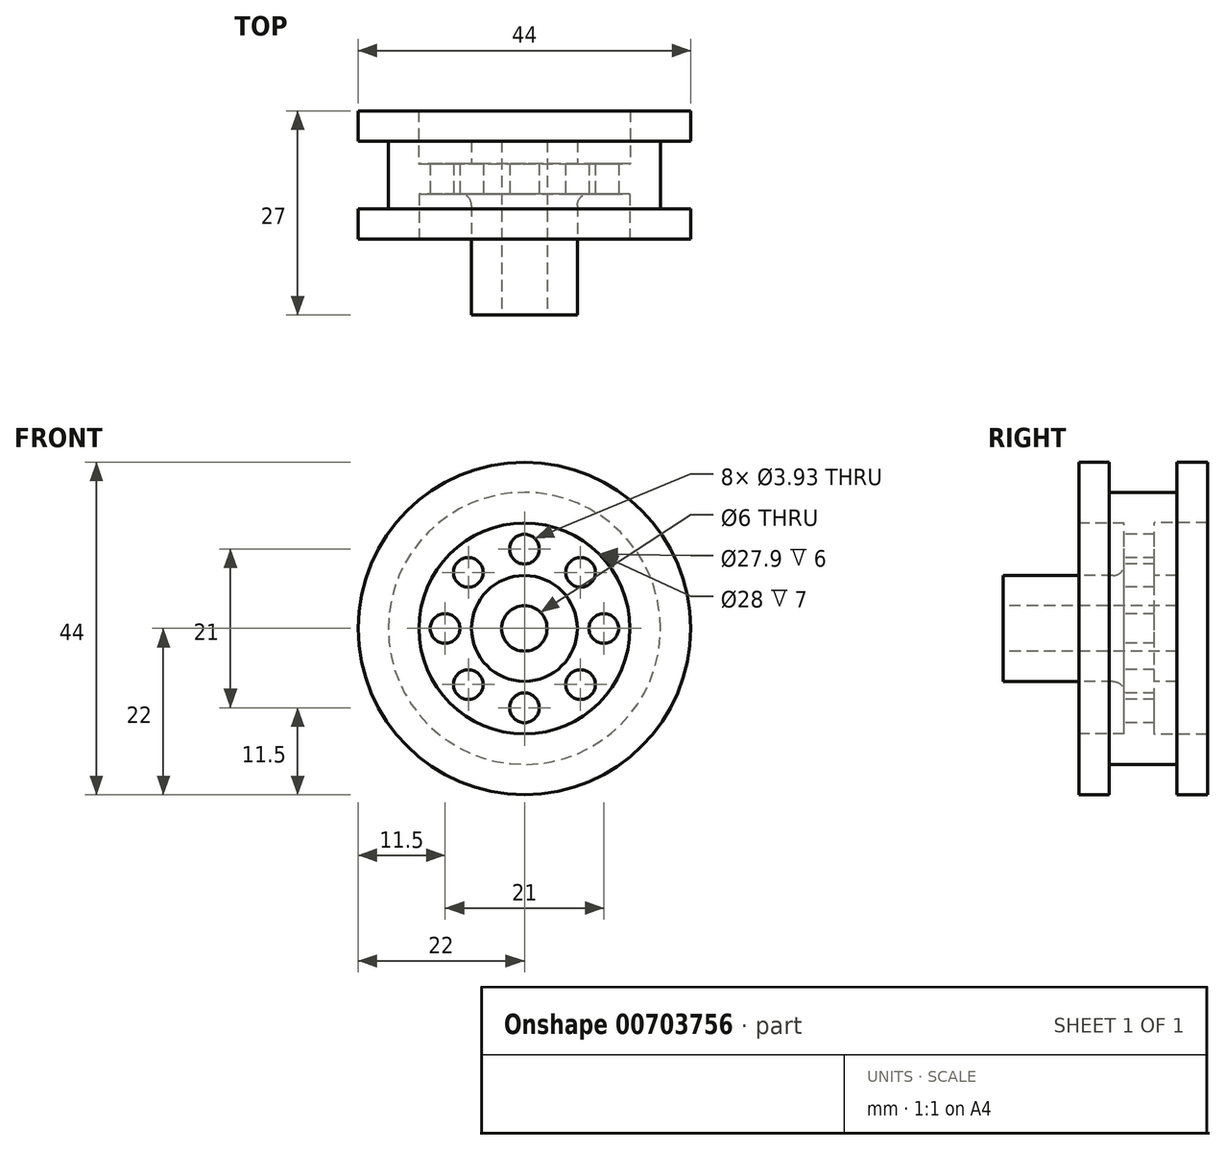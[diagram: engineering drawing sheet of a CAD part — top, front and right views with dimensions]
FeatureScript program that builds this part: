
annotation { "Feature Type Name" : "Feature", "Feature Type Description" : "" }
export const myFeature = defineFeature(function(context is Context, id is Id, definition is map)
    precondition{}
    {
        {
            var Q0;
            Q0=qCreatedBy(makeId("Right.planeOp"),FACE);
            var sketch = newSketch(context, id + "F0", { "sketchPlane" : qUnion([Q0])});
            skLineSegment(sketch, "E0", {"start": v(-26.32, 0) * mm, "end": v(26.14, 0) * mm, "construction": true});
            skLineSegment(sketch, "E1", {"start": v(-10, -3) * mm, "end": v(13, -3) * mm});
            skLineSegment(sketch, "E2", {"start": v(-10, -3) * mm, "end": v(-10, -7) * mm});
            skLineSegment(sketch, "E3", {"start": v(-10, -7) * mm, "end": v(6.25, -7) * mm});
            skLineSegment(sketch, "E4", {"start": v(13, -3) * mm, "end": v(13, -7) * mm});
            skLineSegment(sketch, "E5", {"start": v(13, -7) * mm, "end": v(10, -7) * mm});
            skLineSegment(sketch, "E6", {"start": v(6, -7) * mm, "end": v(6, -13.95) * mm});
            skLineSegment(sketch, "E7", {"start": v(10, -7) * mm, "end": v(10, -14) * mm});
            skLineSegment(sketch, "E8", {"start": v(6, -13.95) * mm, "end": v(0, -13.95) * mm});
            skLineSegment(sketch, "E9", {"start": v(0, -13.95) * mm, "end": v(0, -22) * mm});
            skLineSegment(sketch, "E10", {"start": v(0, -22) * mm, "end": v(4, -22) * mm});
            skLineSegment(sketch, "E11", {"start": v(4, -22) * mm, "end": v(4, -18) * mm});
            skLineSegment(sketch, "E12", {"start": v(4, -18) * mm, "end": v(13, -18) * mm});
            skLineSegment(sketch, "E13", {"start": v(13, -18) * mm, "end": v(13, -22) * mm});
            skLineSegment(sketch, "E14", {"start": v(13, -22) * mm, "end": v(17, -22) * mm});
            skLineSegment(sketch, "E15", {"start": v(17, -22) * mm, "end": v(17, -14) * mm});
            skLineSegment(sketch, "E16", {"start": v(17, -14) * mm, "end": v(10, -14) * mm});
            skSolve(sketch);
        }
        {
            var Q0;
            Q0 = qSketchRegion(id + "F0", true);
            var Q1;
            Q1=sQuery(id+"F0.wireOp",EDGE,"E0");
            revolve(context, id + "F1", {"surfaceOperationType" : NewSurfaceOperationType.NEW, "entities" : qUnion([Q0]), "axis" : qUnion([Q1]), "revolveType" : RevolveType.FULL});
        }
        {
            var Q0;
            Q0=makeQuery(id+"F1.opRevolve","SWEPT_FACE",FACE,{"disambiguationData":[OSD([sQuery(id+"F0.wireOp",EDGE,"E6")])]});
            var sketch = newSketch(context, id + "F2", { "sketchPlane" : qUnion([Q0])});
            skSolve(sketch);
        }
        {
            var Q0;
            {var subQ0=sQuery(id+"F0.wireOp",EDGE,"E6");Q0=makeQuery(id+"F2.imprint","IMPRINT",FACE,{"disambiguationData":[TD([[makeQuery(id+"F2.imprint","IMPRINT",EDGE,{"derivedFrom":makeQuery(id+"F1.opRevolve","SWEPT_EDGE",EDGE,{"disambiguationData":[OSD([sQuery(id+"F0.wireOp",EDGE,"E3"),subQ0])]})}),-1.0]])]});}
            var sketch = newSketch(context, id + "F3", { "sketchPlane" : qUnion([Q0])});
            skCircle(sketch, "E17", {"center": v(10.5, 0) * mm, "radius": 1.97 * mm});
            skCircle(sketch, "E18.1.0", {"center": v(7.42, 7.42) * mm, "radius": 1.97 * mm});
            skCircle(sketch, "E18.2.0", {"center": v(0, 10.5) * mm, "radius": 1.97 * mm});
            skCircle(sketch, "E18.3.0", {"center": v(-7.42, 7.42) * mm, "radius": 1.97 * mm});
            skCircle(sketch, "E18.4.0", {"center": v(-10.5, 0) * mm, "radius": 1.97 * mm});
            skCircle(sketch, "E18.5.0", {"center": v(-7.42, -7.42) * mm, "radius": 1.97 * mm});
            skCircle(sketch, "E18.6.0", {"center": v(0, -10.5) * mm, "radius": 1.97 * mm});
            skCircle(sketch, "E18.7.0", {"center": v(7.42, -7.42) * mm, "radius": 1.97 * mm});
            skPoint(sketch, "E18.center", {"position": v(0, 0) * mm});
            skSolve(sketch);
        }
        {
            var Q0;
            Q0 = qSketchRegion(id + "F3", true);
            extrude(context, id + "F4", {"entities" : qUnion([Q0]), "operationType" : NewBodyOperationType.REMOVE, "endBound" : BoundingType.THROUGH_ALL, "oppositeDirection" : true, "depth" : 25.4 * mm, "offsetDistance" : 25.4 * mm});
        }
        {
            var Q0;
            Q0=makeQuery(id+"F1.opRevolve","SWEPT_EDGE",EDGE,{"disambiguationData":[OSD([sQuery(id+"F0.wireOp",EDGE,"E3"),sQuery(id+"F0.wireOp",EDGE,"E6")])]});
            fillet(context, id + "F5", {"entities" : qUnion([Q0]), "radius" : 1.5 * mm, "tangentPropagation" : true, "allowEdgeOverflow" : false});
        }
    });
